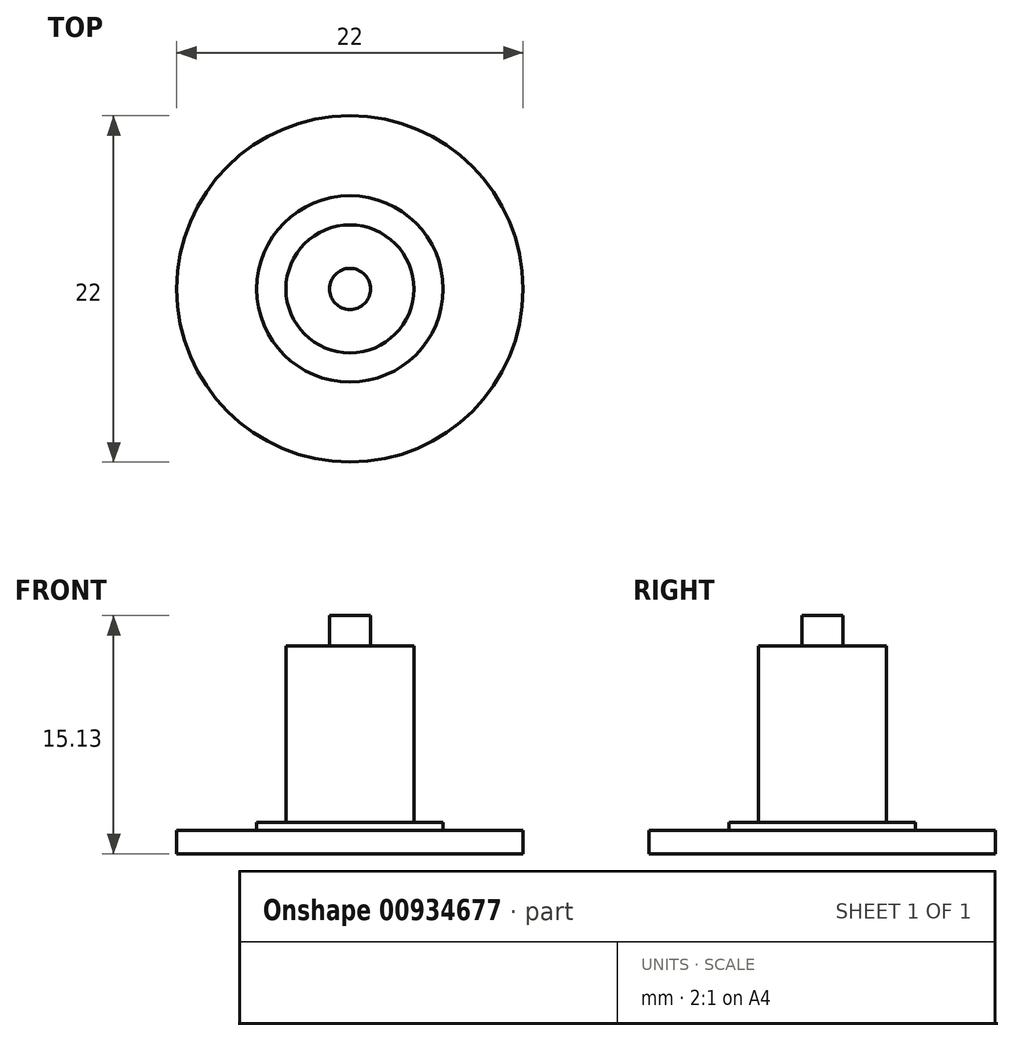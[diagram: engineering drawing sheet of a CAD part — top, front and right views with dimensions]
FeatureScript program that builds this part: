
annotation { "Feature Type Name" : "Feature", "Feature Type Description" : "" }
export const myFeature = defineFeature(function(context is Context, id is Id, definition is map)
    precondition{}
    {
        {
            var Q0;
            Q0=qCreatedBy(makeId("Top.planeOp"),FACE);
            var sketch = newSketch(context, id + "F0", { "sketchPlane" : qUnion([Q0])});
            skCircle(sketch, "E0", {"center": v(0, 0) * mm, "radius": 11 * mm});
            skSolve(sketch);
        }
        {
            var Q0;
            Q0 = qSketchRegion(id + "F0", true);
            extrude(context, id + "F1", {"entities" : qUnion([Q0]), "depth" : 1.5 * mm, "offsetDistance" : 25 * mm});
        }
        {
            var Q0;
            Q0=makeQuery(id+"F1.opExtrude","CAP_FACE",FACE,{"disambiguationData":[OSD([sQuery(id+"F0.wireOp",EDGE,"E0")])],"isStart":false});
            var sketch = newSketch(context, id + "F2", { "sketchPlane" : qUnion([Q0])});
            skCircle(sketch, "E1", {"center": v(0, 0) * mm, "radius": 5.92 * mm});
            skSolve(sketch);
        }
        {
            var Q0;
            Q0 = qSketchRegion(id + "F2", true);
            extrude(context, id + "F3", {"entities" : qUnion([Q0]), "operationType" : NewBodyOperationType.ADD, "depth" : 0.5 * mm, "offsetDistance" : 25 * mm});
        }
        {
            var Q0;
            Q0=makeQuery(id+"F3.opExtrude","CAP_FACE",FACE,{"disambiguationData":[OSD([sQuery(id+"F2.wireOp",EDGE,"E1")])],"isStart":false});
            var sketch = newSketch(context, id + "F4", { "sketchPlane" : qUnion([Q0])});
            skCircle(sketch, "E2", {"center": v(0, 0) * mm, "radius": 4.06 * mm});
            skSolve(sketch);
        }
        {
            var Q0;
            Q0 = qSketchRegion(id + "F4", true);
            extrude(context, id + "F5", {"entities" : qUnion([Q0]), "operationType" : NewBodyOperationType.ADD, "depth" : 11.21 * mm, "offsetDistance" : 25 * mm});
        }
        {
            var Q0;
            Q0=makeQuery(id+"F5.opExtrude","CAP_FACE",FACE,{"disambiguationData":[OSD([sQuery(id+"F4.wireOp",EDGE,"E2")])],"isStart":false});
            var sketch = newSketch(context, id + "F6", { "sketchPlane" : qUnion([Q0])});
            skCircle(sketch, "E3", {"center": v(0, 0) * mm, "radius": 1.3 * mm});
            skSolve(sketch);
        }
        {
            var Q0;
            Q0=makeQuery(id+"F6.imprint","IMPRINT",FACE,{"disambiguationData":[TD([[makeQuery(id+"F6.imprint","IMPRINT",EDGE,{"derivedFrom":sQuery(id+"F6.wireOp",EDGE,"E3")}),1.0]])]});
            extrude(context, id + "F7", {"entities" : qUnion([Q0]), "operationType" : NewBodyOperationType.ADD, "depth" : 1.92 * mm, "offsetDistance" : 25 * mm});
        }
    });
